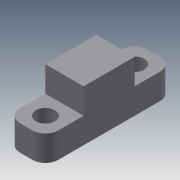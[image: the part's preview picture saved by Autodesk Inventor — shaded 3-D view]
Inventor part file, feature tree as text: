
AUTODESK INVENTOR PART (.ipt)
format: ipt  version: 2015 (Build 190159000, 159)  size: 107,520 bytes
history: native  units: in
note: dims shown in document units (in); Inventor stores cm internally (conversion verified against a paired STEP export)
features: sketch x2, extrude x1, hole x1, fillet x1, mirror x1, projected_geometry x1
ambient origin geometry x8: Origin, YZ Plane, XZ Plane, XY Plane, X Axis, Y Axis, Z Axis, Center Point
bodies: Solid1 (feature_tree)
feature tree (7):
  extrude  "Extrusion1"  Depth=0.75in
  hole  "Hole1"  [1 undecoded]
  fillet  "Fillet1"  Radius=0.75in
  mirror  "Mirror1"
  sketch  "Sketch2"  dims[d0=0.5in d1=0.75in]
  sketch  "Sketch3"  dims[d2=0.5in d3=0.5in d4=0.75in d5=0.0in d6=0.375in d7=0.75in d8=0.375in d9=0.25in d10=0.5635in d11=1.0in d12=0.8108in d13=0.25in]
  projected_geometry  "Projected Loop1"
note: 1 required parameter value undecoded (feature->parameter linkage not recoverable at this tier; creation-order binding heuristic only, values carry confidence <= 0.55)
